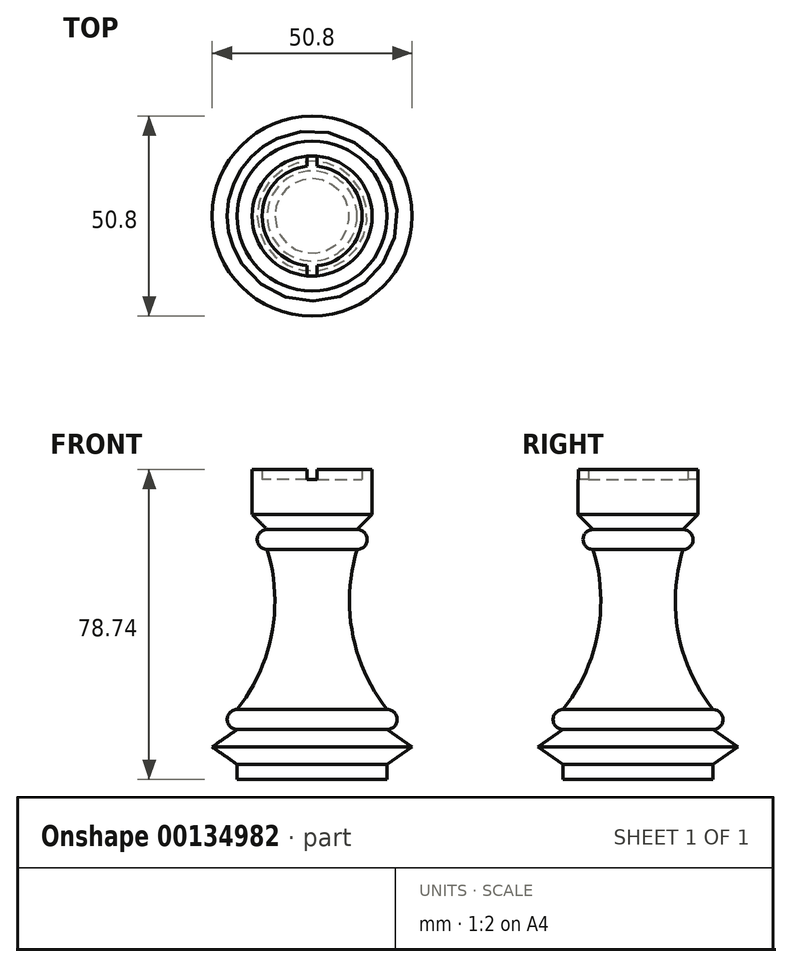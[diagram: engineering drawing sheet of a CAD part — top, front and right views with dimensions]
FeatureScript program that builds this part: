
annotation { "Feature Type Name" : "Feature", "Feature Type Description" : "" }
export const myFeature = defineFeature(function(context is Context, id is Id, definition is map)
    precondition{}
    {
        {
            var Q0;
            Q0=qCreatedBy(makeId("Front.planeOp"),FACE);
            var sketch = newSketch(context, id + "F0", { "sketchPlane" : qUnion([Q0])});
            skLineSegment(sketch, "E0", {"start": v(0, 0) * mm, "end": v(19.05, 0) * mm});
            skLineSegment(sketch, "E1", {"start": v(19.05, 0) * mm, "end": v(19.05, 3.81) * mm});
            skLineSegment(sketch, "E2", {"start": v(19.05, 3.8) * mm, "end": v(25.4, 8.25) * mm});
            skLineSegment(sketch, "E3", {"start": v(25.4, 8.25) * mm, "end": v(19.05, 12.7) * mm});
            skLineSegment(sketch, "E4", {"start": v(0, 0) * mm, "end": v(0, 76.2) * mm});
            skLineSegment(sketch, "E5", {"start": v(0, 76.2) * mm, "end": v(12.7, 76.2) * mm});
            skLineSegment(sketch, "E6", {"start": v(12.7, 76.2) * mm, "end": v(12.7, 78.74) * mm});
            skLineSegment(sketch, "E7", {"start": v(12.7, 78.74) * mm, "end": v(15.24, 78.74) * mm});
            skLineSegment(sketch, "E8", {"start": v(15.24, 78.74) * mm, "end": v(15.24, 67.31) * mm});
            skLineSegment(sketch, "E9", {"start": v(15.24, 67.31) * mm, "end": v(11.43, 63.5) * mm});
            skArc(sketch, "E10", {"start": v(19.05, 12.7) * mm, "mid": v(21.59, 15.24) * mm, "end": v(19.05, 17.78) * mm});
            skArc(sketch, "E11", {"start": v(11.43, 58.42) * mm, "mid": v(13.97, 60.96) * mm, "end": v(11.43, 63.5) * mm});
            skArc(sketch, "E12", {"start": v(11.43, 58.42) * mm, "mid": v(10.23, 37.16) * mm, "end": v(19.05, 17.78) * mm});
            skSolve(sketch);
        }
        {
            var Q0;
            Q0 = qSketchRegion(id + "F0", true);
            var Q1;
            Q1=sQuery(id+"F0.wireOp",EDGE,"E4");
            revolve(context, id + "F1", {"entities" : qUnion([Q0]), "axis" : qUnion([Q1]), "revolveType" : RevolveType.FULL});
        }
        {
            var Q0;
            Q0=qCreatedBy(makeId("Front.planeOp"),FACE);
            var sketch = newSketch(context, id + "F2", { "sketchPlane" : qUnion([Q0])});
            skLineSegment(sketch, "E13.bottom", {"start": v(-1.27, 76.2) * mm, "end": v(1.27, 76.2) * mm});
            skLineSegment(sketch, "E13.top", {"start": v(-1.27, 78.74) * mm, "end": v(1.27, 78.74) * mm});
            skLineSegment(sketch, "E13.left", {"start": v(-1.27, 76.2) * mm, "end": v(-1.27, 78.74) * mm});
            skLineSegment(sketch, "E13.right", {"start": v(1.27, 76.2) * mm, "end": v(1.27, 78.74) * mm});
            skPoint(sketch, "E13.middle", {"position": v(0, 77.47) * mm});
            skSolve(sketch);
        }
        {
            var Q0;
            Q0 = qSketchRegion(id + "F2", true);
            extrude(context, id + "F3", {"entities" : qUnion([Q0]), "operationType" : NewBodyOperationType.REMOVE, "oppositeDirection" : true, "depth" : 25.4 * mm, "hasSecondDirection" : true, "secondDirectionOppositeDirection" : false, "secondDirectionDepth" : 25.4 * mm});
        }
    });
